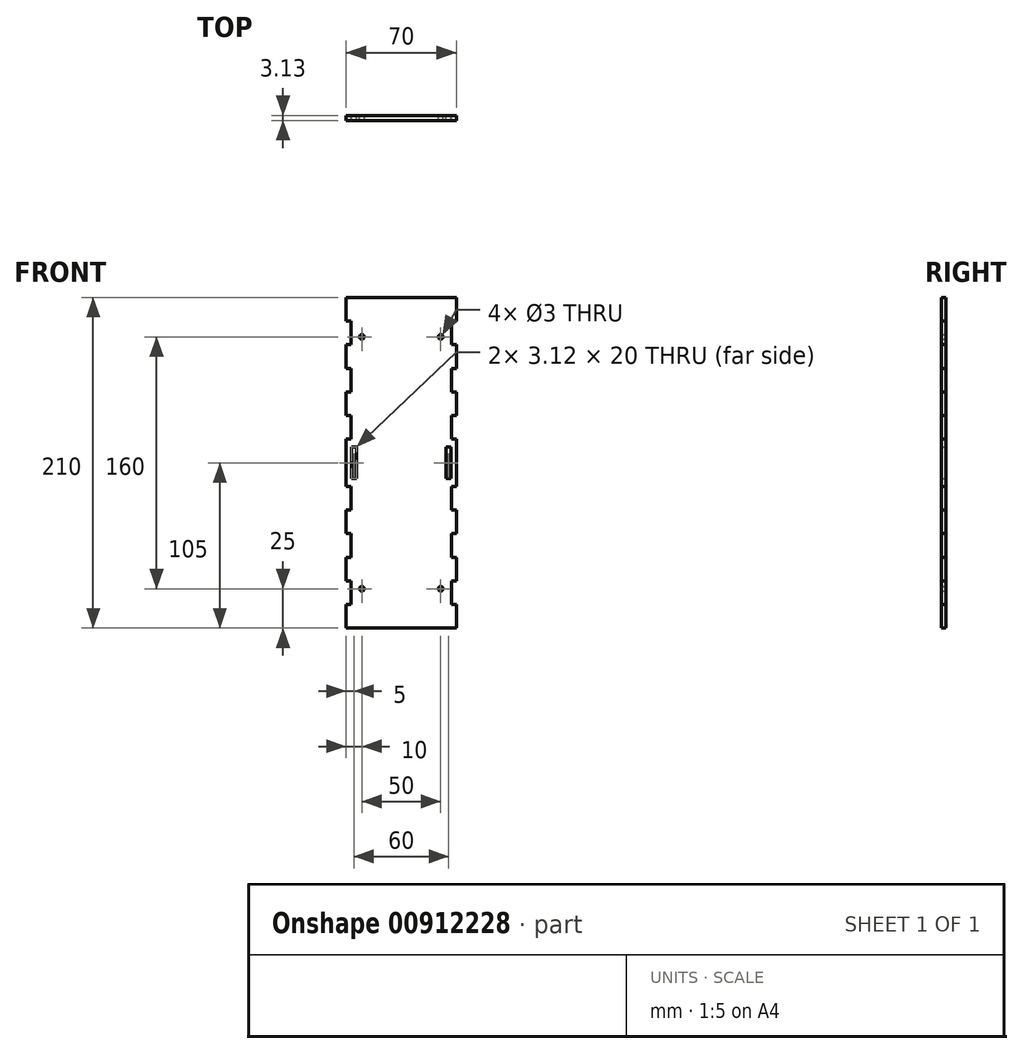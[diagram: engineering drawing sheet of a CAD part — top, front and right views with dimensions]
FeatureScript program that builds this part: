
annotation { "Feature Type Name" : "Feature", "Feature Type Description" : "" }
export const myFeature = defineFeature(function(context is Context, id is Id, definition is map)
    precondition{}
    {
        {
            assignVariable(context, id + "F0", {"name" : "Width", "anyValue" : 3.12});
        }
        {
            var Q0;
            Q0=qCreatedBy(makeId("Front.planeOp"),FACE);
            var sketch = newSketch(context, id + "F1", { "sketchPlane" : qUnion([Q0])});
            skLineSegment(sketch, "E0", {"start": v(0, 0) * mm, "end": v(25, 0) * mm, "construction": true});
            skCircle(sketch, "E1", {"center": v(25, 0) * mm, "radius": 1.5 * mm});
            skLineSegment(sketch, "E2", {"start": v(0, -25) * mm, "end": v(35, -25) * mm});
            skLineSegment(sketch, "E3", {"start": v(35, -25) * mm, "end": v(35, -10) * mm});
            skLineSegment(sketch, "E4", {"start": v(35, -10) * mm, "end": v(31.88, -10) * mm});
            skLineSegment(sketch, "E5", {"start": v(31.88, -10) * mm, "end": v(31.88, 5) * mm});
            skLineSegment(sketch, "E6", {"start": v(31.88, 5) * mm, "end": v(35, 5) * mm});
            skLineSegment(sketch, "E7.1.0.0", {"start": v(31.88, 35) * mm, "end": v(35, 35) * mm});
            skLineSegment(sketch, "E7.1.0.1", {"start": v(31.88, 20) * mm, "end": v(31.88, 35) * mm});
            skLineSegment(sketch, "E7.1.0.2", {"start": v(35, 20) * mm, "end": v(31.88, 20) * mm});
            skLineSegment(sketch, "E7.1.0.3", {"start": v(35, 5) * mm, "end": v(35, 20) * mm});
            skLineSegment(sketch, "E7.2.0.0", {"start": v(31.88, 65) * mm, "end": v(35, 65) * mm});
            skLineSegment(sketch, "E7.2.0.1", {"start": v(31.88, 50) * mm, "end": v(31.88, 65) * mm});
            skLineSegment(sketch, "E7.2.0.2", {"start": v(35, 50) * mm, "end": v(31.88, 50) * mm});
            skLineSegment(sketch, "E7.2.0.3", {"start": v(35, 35) * mm, "end": v(35, 50) * mm});
            skLineSegment(sketch, "E7.direction1", {"start": v(31.88, 5) * mm, "end": v(31.88, 35) * mm, "construction": true});
            skLineSegment(sketch, "E8", {"start": v(35, 65) * mm, "end": v(35, 80) * mm});
            skLineSegment(sketch, "E9", {"start": v(35, 80) * mm, "end": v(0, 80) * mm, "construction": true});
            skLineSegment(sketch, "E10", {"start": v(0, 80) * mm, "end": v(0, 0) * mm, "construction": true});
            skLineSegment(sketch, "E11.MirrorCS", {"start": v(31.88, 155) * mm, "end": v(35, 155) * mm});
            skLineSegment(sketch, "E12.MirrorCS", {"start": v(31.88, 125) * mm, "end": v(35, 125) * mm});
            skLineSegment(sketch, "E13.MirrorCS", {"start": v(31.88, 95) * mm, "end": v(35, 95) * mm});
            skCircle(sketch, "E14.MirrorC", {"center": v(25, 160) * mm, "radius": 1.5 * mm});
            skLineSegment(sketch, "E15.MirrorCS", {"start": v(35, 140) * mm, "end": v(31.88, 140) * mm});
            skLineSegment(sketch, "E16.MirrorCS", {"start": v(35, 170) * mm, "end": v(31.88, 170) * mm});
            skLineSegment(sketch, "E17.MirrorCS", {"start": v(35, 110) * mm, "end": v(31.88, 110) * mm});
            skLineSegment(sketch, "E18.MirrorCS", {"start": v(31.88, 140) * mm, "end": v(31.88, 125) * mm});
            skLineSegment(sketch, "E19.MirrorCS", {"start": v(31.88, 170) * mm, "end": v(31.88, 155) * mm});
            skLineSegment(sketch, "E20.MirrorCS", {"start": v(31.88, 110) * mm, "end": v(31.88, 95) * mm});
            skLineSegment(sketch, "E21.MirrorCS", {"start": v(31.88, 155) * mm, "end": v(31.88, 125) * mm, "construction": true});
            skLineSegment(sketch, "E22.MirrorCS", {"start": v(0, 160) * mm, "end": v(25, 160) * mm, "construction": true});
            skLineSegment(sketch, "E23.MirrorCS", {"start": v(0, 80) * mm, "end": v(0, 160) * mm, "construction": true});
            skLineSegment(sketch, "E24.MirrorCS", {"start": v(35, 125) * mm, "end": v(35, 110) * mm});
            skLineSegment(sketch, "E25.MirrorCS", {"start": v(35, 155) * mm, "end": v(35, 140) * mm});
            skLineSegment(sketch, "E26.MirrorCS", {"start": v(35, 95) * mm, "end": v(35, 80) * mm});
            skLineSegment(sketch, "E27.MirrorCS", {"start": v(0, 185) * mm, "end": v(35, 185) * mm});
            skLineSegment(sketch, "E28.MirrorCS", {"start": v(35, 185) * mm, "end": v(35, 170) * mm});
            skCircle(sketch, "E29.MirrorC", {"center": v(-25, 0) * mm, "radius": 1.5 * mm});
            skLineSegment(sketch, "E30.MirrorCS", {"start": v(-31.88, 35) * mm, "end": v(-35, 35) * mm});
            skLineSegment(sketch, "E31.MirrorCS", {"start": v(-31.88, 5) * mm, "end": v(-35, 5) * mm});
            skLineSegment(sketch, "E32.MirrorCS", {"start": v(-31.88, 20) * mm, "end": v(-31.88, 35) * mm});
            skCircle(sketch, "E33.MirrorC", {"center": v(-25, 160) * mm, "radius": 1.5 * mm});
            skLineSegment(sketch, "E34.MirrorCS", {"start": v(-31.88, 170) * mm, "end": v(-31.88, 155) * mm});
            skLineSegment(sketch, "E35.MirrorCS", {"start": v(-31.88, 125) * mm, "end": v(-35, 125) * mm});
            skLineSegment(sketch, "E36.MirrorCS", {"start": v(-35, 20) * mm, "end": v(-31.88, 20) * mm});
            skLineSegment(sketch, "E37.MirrorCS", {"start": v(-31.88, 155) * mm, "end": v(-35, 155) * mm});
            skLineSegment(sketch, "E38.MirrorCS", {"start": v(-31.88, -10) * mm, "end": v(-31.88, 5) * mm});
            skLineSegment(sketch, "E39.MirrorCS", {"start": v(-35, 110) * mm, "end": v(-31.88, 110) * mm});
            skLineSegment(sketch, "E40.MirrorCS", {"start": v(-35, 5) * mm, "end": v(-35, 20) * mm});
            skLineSegment(sketch, "E41.MirrorCS", {"start": v(-35, 35) * mm, "end": v(-35, 50) * mm});
            skLineSegment(sketch, "E42.MirrorCS", {"start": v(-35, 140) * mm, "end": v(-31.88, 140) * mm});
            skLineSegment(sketch, "E43.MirrorCS", {"start": v(-35, -10) * mm, "end": v(-31.88, -10) * mm});
            skLineSegment(sketch, "E44.MirrorCS", {"start": v(-31.88, 65) * mm, "end": v(-35, 65) * mm});
            skLineSegment(sketch, "E45.MirrorCS", {"start": v(-31.88, 140) * mm, "end": v(-31.88, 125) * mm});
            skLineSegment(sketch, "E46.MirrorCS", {"start": v(-31.88, 5) * mm, "end": v(-31.88, 35) * mm, "construction": true});
            skLineSegment(sketch, "E47.MirrorCS", {"start": v(-31.88, 95) * mm, "end": v(-35, 95) * mm});
            skLineSegment(sketch, "E48.MirrorCS", {"start": v(-31.88, 50) * mm, "end": v(-31.88, 65) * mm});
            skLineSegment(sketch, "E49.MirrorCS", {"start": v(-35, 50) * mm, "end": v(-31.88, 50) * mm});
            skLineSegment(sketch, "E50.MirrorCS", {"start": v(-35, 95) * mm, "end": v(-35, 80) * mm});
            skLineSegment(sketch, "E51.MirrorCS", {"start": v(-35, 170) * mm, "end": v(-31.88, 170) * mm});
            skLineSegment(sketch, "E52.MirrorCS", {"start": v(-35, 125) * mm, "end": v(-35, 110) * mm});
            skLineSegment(sketch, "E53.MirrorCS", {"start": v(-31.88, 110) * mm, "end": v(-31.88, 95) * mm});
            skLineSegment(sketch, "E54.MirrorCS", {"start": v(-35, 185) * mm, "end": v(-35, 170) * mm});
            skLineSegment(sketch, "E55.MirrorCS", {"start": v(-35, 155) * mm, "end": v(-35, 140) * mm});
            skLineSegment(sketch, "E56.MirrorCS", {"start": v(-35, 65) * mm, "end": v(-35, 80) * mm});
            skLineSegment(sketch, "E57.MirrorCS", {"start": v(-35, -25) * mm, "end": v(-35, -10) * mm});
            skLineSegment(sketch, "E58.MirrorCS", {"start": v(-31.88, 155) * mm, "end": v(-31.88, 125) * mm, "construction": true});
            skLineSegment(sketch, "E59.MirrorCS", {"start": v(0, -25) * mm, "end": v(-35, -25) * mm});
            skLineSegment(sketch, "E60.MirrorCS", {"start": v(0, 0) * mm, "end": v(-25, 0) * mm, "construction": true});
            skLineSegment(sketch, "E61.MirrorCS", {"start": v(0, 185) * mm, "end": v(-35, 185) * mm});
            skLineSegment(sketch, "E62.MirrorCS", {"start": v(0, 160) * mm, "end": v(-25, 160) * mm, "construction": true});
            skLineSegment(sketch, "E63.MirrorCS", {"start": v(-35, 80) * mm, "end": v(0, 80) * mm, "construction": true});
            skLineSegment(sketch, "E64.bottom", {"start": v(31.56, 70) * mm, "end": v(28.44, 70) * mm});
            skLineSegment(sketch, "E64.top", {"start": v(31.56, 90) * mm, "end": v(28.44, 90) * mm});
            skLineSegment(sketch, "E64.left", {"start": v(31.56, 70) * mm, "end": v(31.56, 90) * mm});
            skLineSegment(sketch, "E64.right", {"start": v(28.44, 70) * mm, "end": v(28.44, 90) * mm});
            skPoint(sketch, "E64.middle", {"position": v(30, 80) * mm});
            skPoint(sketch, "E65.MirrorP", {"position": v(-30, 80) * mm});
            skLineSegment(sketch, "E66.MirrorCS", {"start": v(-31.56, 90) * mm, "end": v(-28.44, 90) * mm});
            skLineSegment(sketch, "E67.MirrorCS", {"start": v(-31.56, 70) * mm, "end": v(-28.44, 70) * mm});
            skLineSegment(sketch, "E68.MirrorCS", {"start": v(-28.44, 70) * mm, "end": v(-28.44, 90) * mm});
            skLineSegment(sketch, "E69.MirrorCS", {"start": v(-31.56, 70) * mm, "end": v(-31.56, 90) * mm});
            skSolve(sketch);
        }
        {
            var Q0;
            Q0=qSketchRegion(id+"F1",true);
            extrude(context, id + "F2", {"entities" : qUnion([Q0]), "depth" : (getVariable(context, 'Width')) * mm, "offsetDistance" : 25 * mm});
        }
    });
